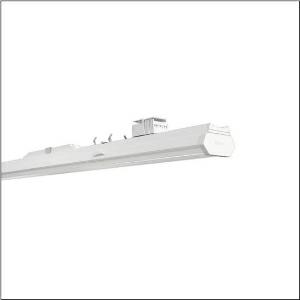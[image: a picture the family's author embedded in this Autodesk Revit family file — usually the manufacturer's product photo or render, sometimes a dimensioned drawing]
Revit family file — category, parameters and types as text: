
# Revit family: licross_r__11_protected_mo_51ts12dn48xf3s_f20f
name_source: partatom
category: Lighting Fixtures
units: mm (PartAtom-declared; Revit-internal decimal feet)

## family parameters
Cut with Voids When Loaded = No
Host = Face
Light Source = No
Part Type = Normal
Room Calculation Point = No
Round Connector Dimension = Use Diameter
Shared = No

## types (1)
- --- (1 x LED, 810 lm, 5 W, 4000K)
    Apparent Load = 5 VA
    CIE Flux Codes = 54 82 95 97 100
    Color Rendering = 80
    Color Temperature = 4000K
    Default Elevation = 1800 mm
    Description = Licross® 11 Protected MO, luminaire insert, of sheet steel, galvanised, coil coated, white, length: 1.500mm, width: 90mm, height: 101mm, LED rated luminous flux: 8.470lm, light colour: 840, control gear: DALI 2, control gear: ECG DALI, with plug, 6-pole, with phase selection, for trunking rail, 14-core, mains connection: 220..240V, AC/DC, 0/50..60Hz, halogen-free wiring, for emergency light function, converter,control gear: single battery element, battery: LiFeP04, 9Ah, primary optical cover: cover, of PMMA, light emission: direct with ceiling illumination distribution, protection rating (complete): IP50, insulation class (complete): insulation class I (protective earthing), certification: CE, UKCA, protection symbol: D if used in an environment with non-conductive dust loads with corresponding accessories, permissible ambient temperature for indoor applications: +5..+35°C, standard: EN 60598-2-22, corresponds to IFS (International Featured Standards) requirements for safety and quality in the food industry, reducing of maximum allowable ambient temperature of 5°C with ceiling mounting, LABS conformity tested according to VDMA 24364:2018-05, packaging unit: 1 piece
    Height = 92 mm
    Lamp = 1 x LED
    Lamp Light Flux = 810 lm
    Lamp Power = 5 W
    Lamp count = 1
    Length = 1500 mm
    Luminous efficacy = 162 lm/W
    Manufacturer = Siteco
    ModVariant = No
    Model = 51TS12DN48XF3S
    Mounting Place = Ceiling
    Mounting Type = Pendant
    Number of Poles = 1
    OnlyDefault = Yes
    Power Factor = 1
    Product Name = Licross® 11 Protected MO
    Product group = luminaire insert
    ProductGroupID = 902
    Protection Class = Protection class I
    Protection Degree = IP 50
    RLX_Detail_Level = 1
    RlxData = <blob elided: 24705 chars, md5=71aad837>
    Socket = socket
    Standby Power = 0 W
    System Light Flux = 810 lm
    System Power = 5 W
    Type Comments = : emergency light operation: 3 h
    Type Image = l_1256145.jpg
    URL = http://relux.com
    VarID = @adj_126211
    Voltage = 0 V
    Weight = 0.00 kg
    Width = 88 mm

## geometry (parser evidence)
native form markers: Blend x4, Sweep x10
no freeform markers — native parametric forms only
